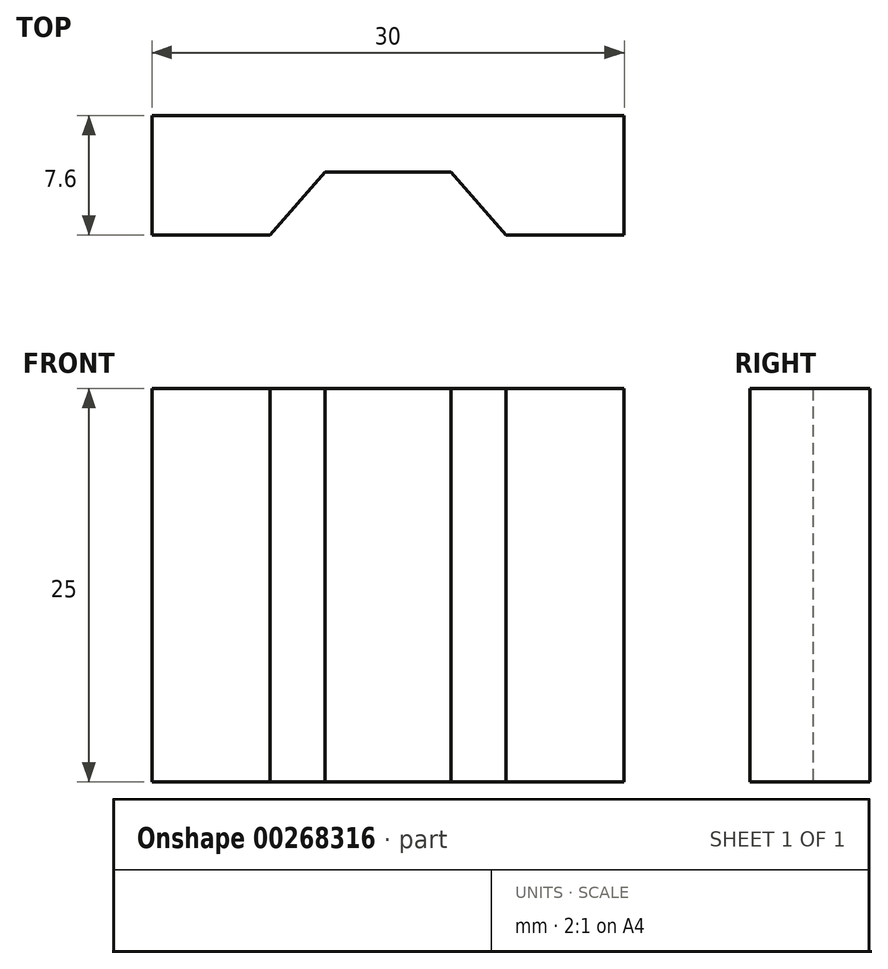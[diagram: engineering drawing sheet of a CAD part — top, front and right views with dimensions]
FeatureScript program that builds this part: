
annotation { "Feature Type Name" : "Feature", "Feature Type Description" : "" }
export const myFeature = defineFeature(function(context is Context, id is Id, definition is map)
    precondition{}
    {
        {
            var Q0;
            Q0=qCreatedBy(makeId("Top.planeOp"),FACE);
            var sketch = newSketch(context, id + "F0", { "sketchPlane" : qUnion([Q0])});
            skLineSegment(sketch, "E0.bottom", {"start": v(-18.16, 10.65) * mm, "end": v(11.84, 10.65) * mm});
            skLineSegment(sketch, "E0.top", {"start": v(-18.16, 3.05) * mm, "end": v(-10.66, 3.05) * mm});
            skLineSegment(sketch, "E0.left", {"start": v(-18.16, 10.65) * mm, "end": v(-18.16, 3.05) * mm});
            skLineSegment(sketch, "E0.right", {"start": v(11.84, 10.65) * mm, "end": v(11.84, 3.05) * mm});
            skLineSegment(sketch, "E1", {"start": v(-7.16, 7.05) * mm, "end": v(0.84, 7.05) * mm});
            skPoint(sketch, "E2", {"position": v(-10.66, 3.05) * mm});
            skPoint(sketch, "E3", {"position": v(4.34, 3.05) * mm});
            skLineSegment(sketch, "E4", {"start": v(-10.66, 3.05) * mm, "end": v(-7.16, 7.05) * mm});
            skLineSegment(sketch, "E5", {"start": v(4.34, 3.05) * mm, "end": v(0.84, 7.05) * mm});
            skLineSegment(sketch, "E6.trimOffspring", {"start": v(4.34, 3.05) * mm, "end": v(11.84, 3.05) * mm});
            skSolve(sketch);
        }
        {
            var Q0;
            Q0=makeQuery(id+"F0.imprint","IMPRINT",FACE,{"disambiguationData":[TD([[makeQuery(id+"F0.imprint","IMPRINT",EDGE,{"derivedFrom":sQuery(id+"F0.wireOp",EDGE,"E0.bottom")}),-1.0]])]});
            extrude(context, id + "F1", {"entities" : qUnion([Q0]), "depth" : 25 * mm});
        }
    });
